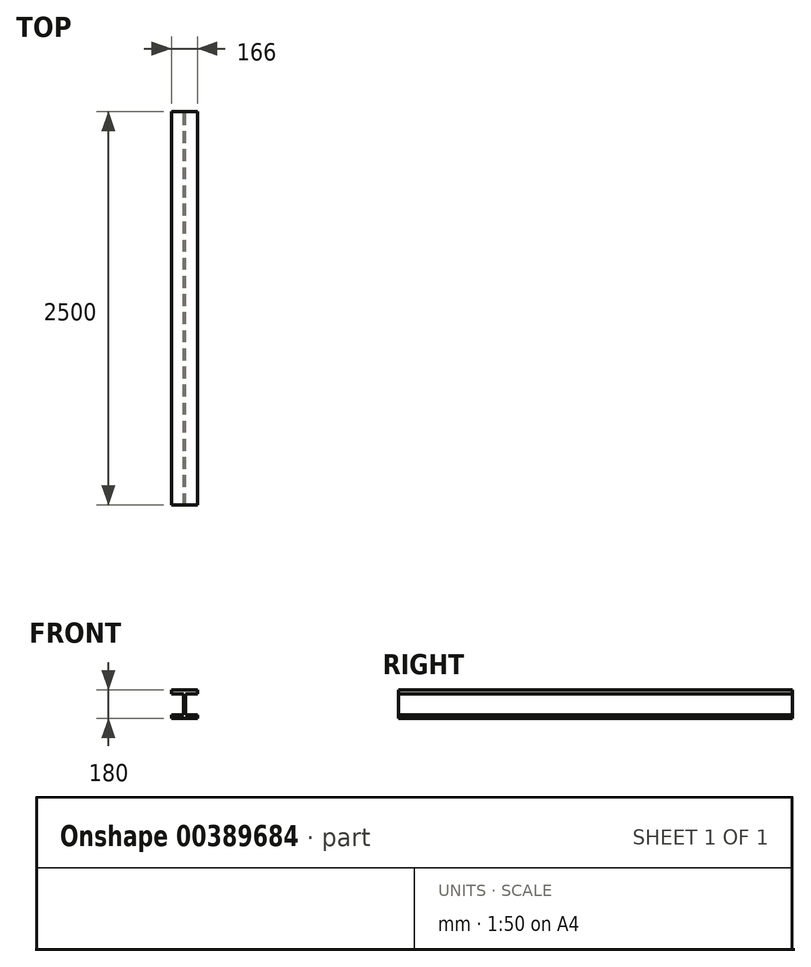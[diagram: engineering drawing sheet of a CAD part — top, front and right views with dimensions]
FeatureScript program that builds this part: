
annotation { "Feature Type Name" : "Feature", "Feature Type Description" : "" }
export const myFeature = defineFeature(function(context is Context, id is Id, definition is map)
    precondition{}
    {
        {
            var Q0;
            Q0=qCreatedBy(makeId("Front.planeOp"),FACE);
            var sketch = newSketch(context, id + "F0", { "sketchPlane" : qUnion([Q0])});
            skLineSegment(sketch, "E0", {"start": v(-83, 90) * mm, "end": v(83, 90) * mm});
            skLineSegment(sketch, "E1.MirrorCS", {"start": v(-83, -90) * mm, "end": v(83, -90) * mm});
            skLineSegment(sketch, "E2", {"start": v(-83, 90) * mm, "end": v(-83, 67) * mm});
            skLineSegment(sketch, "E3", {"start": v(-83, 67) * mm, "end": v(-7, 67) * mm});
            skLineSegment(sketch, "E4", {"start": v(-7, 67) * mm, "end": v(-7, -67) * mm});
            skLineSegment(sketch, "E5.MirrorCS", {"start": v(-83, -90) * mm, "end": v(-83, -67) * mm});
            skLineSegment(sketch, "E6.MirrorCS", {"start": v(-83, -67) * mm, "end": v(-7, -67) * mm});
            skLineSegment(sketch, "E7.MirrorCS", {"start": v(83, 67) * mm, "end": v(7, 67) * mm});
            skLineSegment(sketch, "E8.MirrorCS", {"start": v(83, 90) * mm, "end": v(83, 67) * mm});
            skLineSegment(sketch, "E9.MirrorCS", {"start": v(7, 67) * mm, "end": v(7, -67) * mm});
            skLineSegment(sketch, "E10.MirrorCS", {"start": v(83, -67) * mm, "end": v(7, -67) * mm});
            skLineSegment(sketch, "E11.MirrorCS", {"start": v(83, -90) * mm, "end": v(83, -67) * mm});
            skSolve(sketch);
        }
        {
            var Q0;
            Q0=makeQuery(id+"F0.imprint","IMPRINT",FACE,{"disambiguationData":[TD([[makeQuery(id+"F0.imprint","IMPRINT",EDGE,{"derivedFrom":sQuery(id+"F0.wireOp",EDGE,"E0")}),-1.0]])]});
            extrude(context, id + "F1", {"entities" : qUnion([Q0]), "endBound" : BoundingType.SYMMETRIC, "depth" : 2500 * mm});
        }
    });
